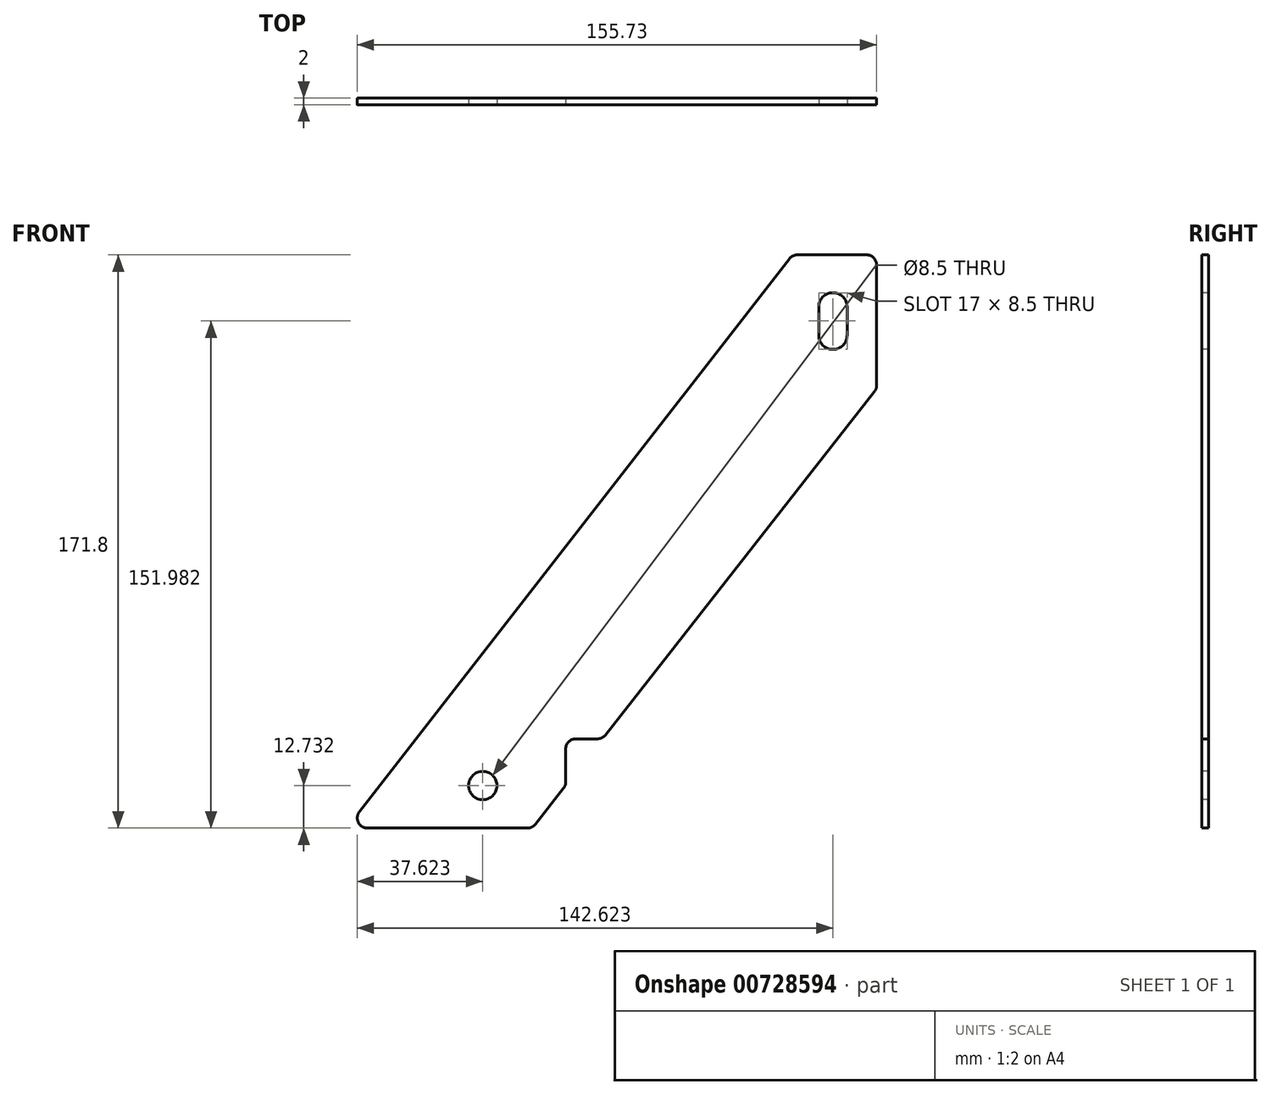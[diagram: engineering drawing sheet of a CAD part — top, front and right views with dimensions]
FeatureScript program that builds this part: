
annotation { "Feature Type Name" : "Feature", "Feature Type Description" : "" }
export const myFeature = defineFeature(function(context is Context, id is Id, definition is map)
    precondition{}
    {
        {
            var Q0;
            Q0=qCreatedBy(makeId("Front.planeOp"),FACE);
            var sketch = newSketch(context, id + "F0", { "sketchPlane" : qUnion([Q0])});
            skCircle(sketch, "E0", {"center": v(-49.16, -75.35) * mm, "radius": 4.25 * mm});
            skArc(sketch, "E1", {"start": v(51.6, 59.65) * mm, "mid": v(55.84, 55.4) * mm, "end": v(60.1, 59.65) * mm});
            skLineSegment(sketch, "E2", {"start": v(-83.78, -88.08) * mm, "end": v(-35.72, -88.08) * mm});
            skLineSegment(sketch, "E3", {"start": v(-86.15, -83.24) * mm, "end": v(42.81, 82.56) * mm});
            skLineSegment(sketch, "E4", {"start": v(68.95, 80.72) * mm, "end": v(68.95, 44.6) * mm});
            skPoint(sketch, "E5.orphan", {"position": v(-34.26, -88.08) * mm});
            skLineSegment(sketch, "E6", {"start": v(65.95, 83.72) * mm, "end": v(45.18, 83.72) * mm});
            skLineSegment(sketch, "E7", {"start": v(-33.36, -86.93) * mm, "end": v(-24.92, -76.16) * mm});
            skArc(sketch, "E8", {"start": v(60.1, 68.15) * mm, "mid": v(55.84, 72.4) * mm, "end": v(51.6, 68.15) * mm});
            skLineSegment(sketch, "E9", {"start": v(51.6, 68.15) * mm, "end": v(51.6, 59.65) * mm});
            skLineSegment(sketch, "E10", {"start": v(60.1, 68.15) * mm, "end": v(60.1, 59.65) * mm});
            skLineSegment(sketch, "E11", {"start": v(-24.28, -74.31) * mm, "end": v(-24.28, -64.35) * mm});
            skLineSegment(sketch, "E12", {"start": v(-21.28, -61.35) * mm, "end": v(-14.76, -61.35) * mm});
            skLineSegment(sketch, "E13.trimOffspring", {"start": v(-12.4, -60.2) * mm, "end": v(68.3, 42.75) * mm});
            skPoint(sketch, "E14.visualSharp", {"position": v(-24.28, -61.35) * mm});
            skArc(sketch, "E14.filletArc", {"start": v(-21.28, -61.35) * mm, "mid": v(-23.4, -62.23) * mm, "end": v(-24.28, -64.35) * mm});
            skPoint(sketch, "E15.visualSharp", {"position": v(-13.3, -61.35) * mm});
            skArc(sketch, "E15.filletArc", {"start": v(-14.76, -61.35) * mm, "mid": v(-13.45, -61.05) * mm, "end": v(-12.4, -60.2) * mm});
            skArc(sketch, "E16.filletArc", {"start": v(-35.72, -88.08) * mm, "mid": v(-34.4, -87.78) * mm, "end": v(-33.36, -86.93) * mm});
            skPoint(sketch, "E17.visualSharp", {"position": v(-24.28, -75.35) * mm});
            skArc(sketch, "E17.filletArc", {"start": v(-24.92, -76.16) * mm, "mid": v(-24.44, -75.3) * mm, "end": v(-24.28, -74.31) * mm});
            skPoint(sketch, "E18.visualSharp", {"position": v(-89.91, -88.08) * mm});
            skArc(sketch, "E18.filletArc", {"start": v(-86.15, -83.24) * mm, "mid": v(-86.47, -86.4) * mm, "end": v(-83.78, -88.08) * mm});
            skPoint(sketch, "E19.visualSharp", {"position": v(68.95, 83.72) * mm});
            skArc(sketch, "E19.filletArc", {"start": v(68.95, 80.72) * mm, "mid": v(68.07, 82.84) * mm, "end": v(65.95, 83.72) * mm});
            skPoint(sketch, "E20.visualSharp", {"position": v(43.71, 83.72) * mm});
            skArc(sketch, "E20.filletArc", {"start": v(45.18, 83.72) * mm, "mid": v(43.86, 83.42) * mm, "end": v(42.81, 82.56) * mm});
            skPoint(sketch, "E21.visualSharp", {"position": v(68.95, 43.57) * mm});
            skArc(sketch, "E21.filletArc", {"start": v(68.3, 42.75) * mm, "mid": v(68.78, 43.62) * mm, "end": v(68.95, 44.6) * mm});
            skSolve(sketch);
        }
        {
            var Q0;
            Q0 = qSketchRegion(id + "F0", true);
            extrude(context, id + "F1", {"entities" : qUnion([Q0]), "oppositeDirection" : true, "depth" : 2 * mm, "offsetDistance" : 25 * mm});
        }
    });
